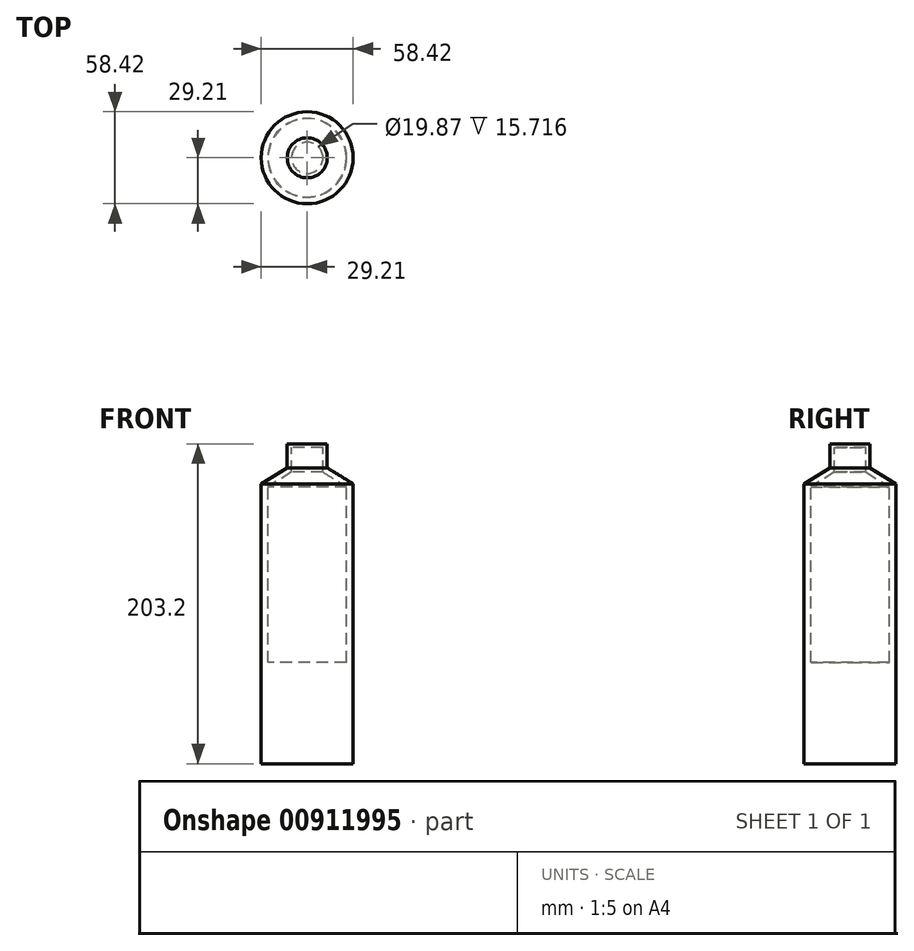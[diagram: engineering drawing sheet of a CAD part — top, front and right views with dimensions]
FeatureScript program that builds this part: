
annotation { "Feature Type Name" : "Feature", "Feature Type Description" : "" }
export const myFeature = defineFeature(function(context is Context, id is Id, definition is map)
    precondition{}
    {
        {
            var Q0;
            Q0=qCreatedBy(makeId("Front.planeOp"),FACE);
            var sketch = newSketch(context, id + "F0", { "sketchPlane" : qUnion([Q0])});
            skLineSegment(sketch, "E0", {"start": v(0, 118.1) * mm, "end": v(0, -85.1) * mm, "construction": true});
            skLineSegment(sketch, "E1", {"start": v(0, -85.1) * mm, "end": v(29.21, -85.1) * mm});
            skLineSegment(sketch, "E2", {"start": v(29.21, -85.1) * mm, "end": v(29.21, 92.7) * mm});
            skLineSegment(sketch, "E3", {"start": v(0, 118.1) * mm, "end": v(12.7, 118.1) * mm});
            skLineSegment(sketch, "E4", {"start": v(12.7, 118.1) * mm, "end": v(12.7, 102.86) * mm});
            skLineSegment(sketch, "E5", {"start": v(12.7, 102.86) * mm, "end": v(29.21, 92.7) * mm});
            skLineSegment(sketch, "E6", {"start": v(0, 115.86) * mm, "end": v(9.94, 115.86) * mm});
            skLineSegment(sketch, "E7", {"start": v(9.94, 115.86) * mm, "end": v(9.94, 100.15) * mm});
            skLineSegment(sketch, "E8", {"start": v(9.94, 100.15) * mm, "end": v(25.04, 90.86) * mm});
            skLineSegment(sketch, "E9", {"start": v(0, 118.1) * mm, "end": v(0, 115.86) * mm});
            skLineSegment(sketch, "E10", {"start": v(0, -85.1) * mm, "end": v(0, -20.88) * mm});
            skLineSegment(sketch, "E11", {"start": v(0, -20.88) * mm, "end": v(24.87, -20.88) * mm});
            skLineSegment(sketch, "E12", {"start": v(24.87, -20.88) * mm, "end": v(25.04, 90.86) * mm});
            skSolve(sketch);
        }
        {
            var Q0;
            Q0=makeQuery(id+"F0.imprint","IMPRINT",FACE,{"disambiguationData":[TD([[makeQuery(id+"F0.imprint","IMPRINT",EDGE,{"derivedFrom":sQuery(id+"F0.wireOp",EDGE,"E1")}),1.0]])]});
            var Q1;
            Q1=sQuery(id+"F0.wireOp",EDGE,"E0");
            revolve(context, id + "F1", {"surfaceOperationType" : NewSurfaceOperationType.NEW, "entities" : qUnion([Q0]), "axis" : qUnion([Q1]), "revolveType" : RevolveType.ONE_DIRECTION, "angle" : 360 * degree});
        }
    });
